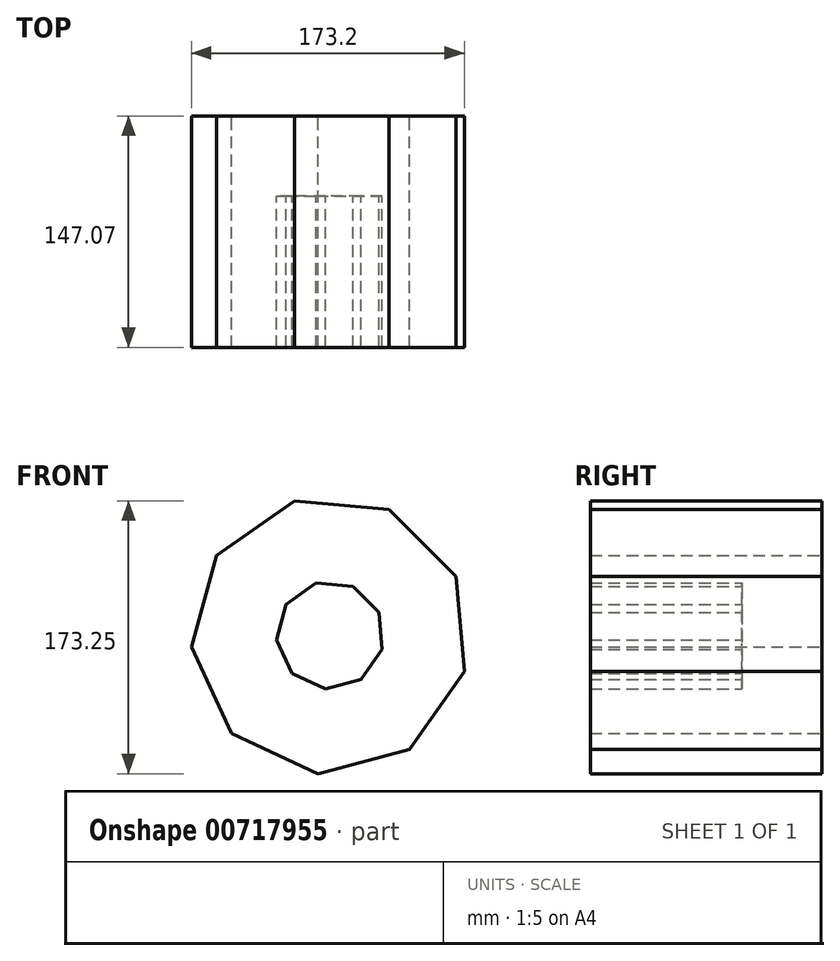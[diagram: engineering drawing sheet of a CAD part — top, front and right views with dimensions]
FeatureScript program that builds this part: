
annotation { "Feature Type Name" : "Feature", "Feature Type Description" : "" }
export const myFeature = defineFeature(function(context is Context, id is Id, definition is map)
    precondition{}
    {
        {
            var Q0;
            Q0=qCreatedBy(makeId("Front.planeOp"),FACE);
            var sketch = newSketch(context, id + "F0", { "sketchPlane" : qUnion([Q0])});
            skCircle(sketch, "E0.cCircle", {"center": v(0, 0) * mm, "radius": 82.96 * mm, "construction": true});
            skLineSegment(sketch, "E0.0", {"start": v(-62.52, -62.33) * mm, "end": v(-87.96, -7.56) * mm});
            skLineSegment(sketch, "E0.1", {"start": v(-87.96, -7.56) * mm, "end": v(-72.24, 50.75) * mm});
            skLineSegment(sketch, "E0.2", {"start": v(-72.24, 50.75) * mm, "end": v(-22.72, 85.31) * mm});
            skLineSegment(sketch, "E0.3", {"start": v(-22.72, 85.31) * mm, "end": v(37.43, 79.96) * mm});
            skLineSegment(sketch, "E0.4", {"start": v(37.43, 79.96) * mm, "end": v(80.07, 37.2) * mm});
            skLineSegment(sketch, "E0.5", {"start": v(80.07, 37.2) * mm, "end": v(85.24, -22.98) * mm});
            skLineSegment(sketch, "E0.6", {"start": v(85.24, -22.98) * mm, "end": v(50.53, -72.4) * mm});
            skLineSegment(sketch, "E0.7", {"start": v(50.53, -72.4) * mm, "end": v(-7.83, -87.94) * mm});
            skLineSegment(sketch, "E0.8", {"start": v(-7.83, -87.94) * mm, "end": v(-62.52, -62.33) * mm});
            skPoint(sketch, "E0.0.midPoint", {"position": v(-75.24, -34.95) * mm});
            skSolve(sketch);
        }
        {
            var Q0;
            Q0=makeQuery(id+"F0.imprint","IMPRINT",FACE,{"disambiguationData":[TD([[makeQuery(id+"F0.imprint","IMPRINT",EDGE,{"derivedFrom":sQuery(id+"F0.wireOp",EDGE,"E0.0")}),-1.0]])]});
            extrude(context, id + "F1", {"entities" : qUnion([Q0]), "depth" : 147.07 * mm, "offsetDistance" : 25.4 * mm});
        }
        {
            var Q0;
            Q0=makeQuery(id+"F1.opExtrude","CAP_FACE",FACE,{"disambiguationData":[OSD([sQuery(id+"F0.wireOp",EDGE,"E0.0"),sQuery(id+"F0.wireOp",EDGE,"E0.1"),sQuery(id+"F0.wireOp",EDGE,"E0.2"),sQuery(id+"F0.wireOp",EDGE,"E0.3"),sQuery(id+"F0.wireOp",EDGE,"E0.4"),sQuery(id+"F0.wireOp",EDGE,"E0.5"),sQuery(id+"F0.wireOp",EDGE,"E0.6"),sQuery(id+"F0.wireOp",EDGE,"E0.7"),sQuery(id+"F0.wireOp",EDGE,"E0.8")])],"isStart":false});
            shell(context, id + "F2", {"entities" : qUnion([Q0]), "thickness" : 50.8 * mm});
        }
    });
